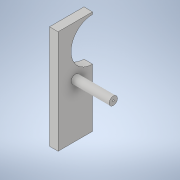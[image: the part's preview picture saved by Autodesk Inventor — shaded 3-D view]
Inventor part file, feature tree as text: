
AUTODESK INVENTOR PART (.ipt)
format: ipt  version: 2021 (Build 250183000, 183)  size: 131,072 bytes
history: native  units: in
note: dims shown in document units (in); Inventor stores cm internally (conversion verified against a paired STEP export)
features: extrude x3, sketch x3, projected_geometry x1
ambient origin geometry x8: Origin, YZ Plane, XZ Plane, XY Plane, X Axis, Y Axis, Z Axis, Center Point
bodies: Solid1 (feature_tree)
feature tree (7):
  extrude  "Extrusion1"  Depth=1.0in
  extrude  "Extrusion2"  Depth=0.625in
  extrude  "Extrusion4"  Depth=0.1in
  sketch  "Sketch1"  dims[d0=3.0in d1=1.0in]
  sketch  "Sketch2"  dims[d2=1.25in d3=0.625in]
  sketch  "Sketch4"  dims[d4=0.25in d5=0.0in d6=0.1in d7=1.0in d8=0.5in d9=0.35in d10=1.5in d11=0.0in d16=0.05in d17=0.24in d18=1.1in d19=0.0in d20=0.0625in]
  projected_geometry  "Projected Loop2"
